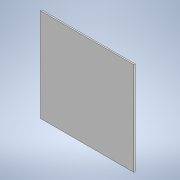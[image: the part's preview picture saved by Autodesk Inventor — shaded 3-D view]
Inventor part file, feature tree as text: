
AUTODESK INVENTOR PART (.ipt)
format: ipt  version: 2020.1 (Build 241239000, 239)  size: 140,800 bytes
history: native  units: in
note: dims shown in document units (in); Inventor stores cm internally (conversion verified against a paired STEP export)
features: extrude x5, sketch x5
ambient origin geometry x8: Origin, YZ Plane, XZ Plane, XY Plane, X Axis, Y Axis, Z Axis, Center Point
bodies: Solid1 (feature_tree)
feature tree (10):
  extrude  "Extrusion1"  Depth=2.5591in
  extrude  "Extrusion2"  Depth=0.0394in TaperAngle=0.0deg
  sketch  "Sketch3"  dims[d18=0.0394in d19=0.0in d23=1.811in]
  extrude  "Extrusion5"  Depth=0.0394in
  extrude  "Extrusion6"  Depth=0.1181in TaperAngle=0.0deg
  extrude  "Extrusion7"  [1 undecoded]
  sketch  "Sketch1"  dims[d0=2.5591in d1=2.5591in]
  sketch  "Sketch2"  dims[d2=0.0906in d3=0.0in d5=0.0394in d6=0.0in]
  sketch  "Sketch6"  dims[d24=0.1181in d25=0.0in d29=0.1181in d30=0.0in]
  sketch  "Sketch7"
note: 1 required parameter value undecoded (feature->parameter linkage not recoverable at this tier; creation-order binding heuristic only, values carry confidence <= 0.55)
